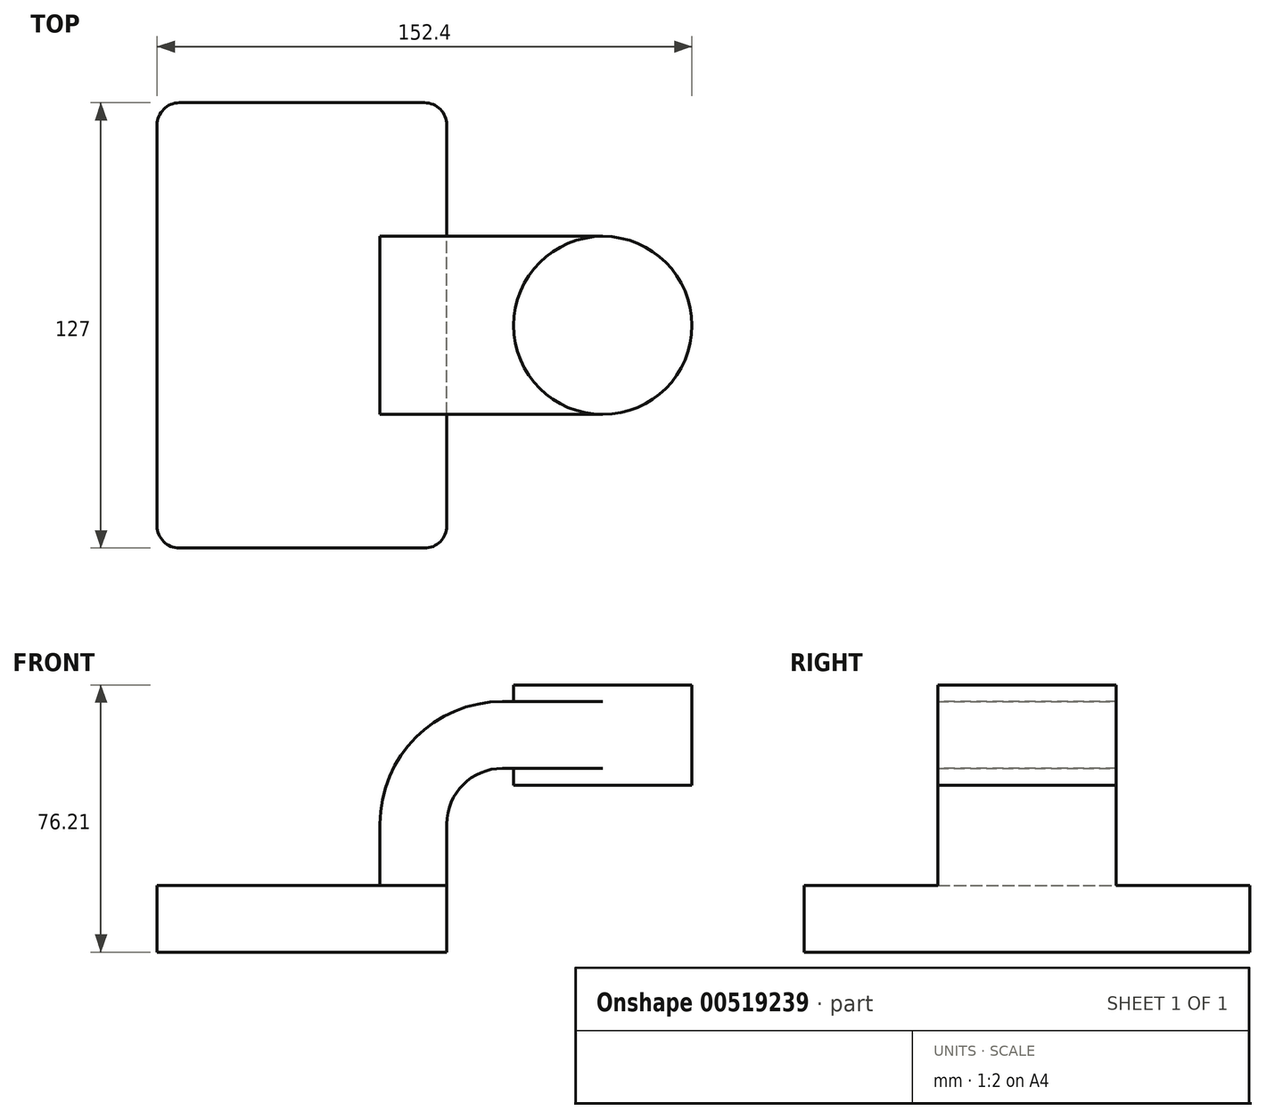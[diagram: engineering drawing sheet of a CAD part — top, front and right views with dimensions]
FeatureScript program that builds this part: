
annotation { "Feature Type Name" : "Feature", "Feature Type Description" : "" }
export const myFeature = defineFeature(function(context is Context, id is Id, definition is map)
    precondition{}
    {
        {
            var Q0;
            Q0=qCreatedBy(makeId("Front.planeOp"),FACE);
            var sketch = newSketch(context, id + "F0", { "sketchPlane" : qUnion([Q0])});
            skLineSegment(sketch, "E0.bottom", {"start": v(-41.27, -9.53) * mm, "end": v(41.28, -9.53) * mm});
            skLineSegment(sketch, "E0.top", {"start": v(-41.28, 9.53) * mm, "end": v(41.28, 9.53) * mm});
            skLineSegment(sketch, "E0.left", {"start": v(-41.28, -9.53) * mm, "end": v(-41.28, 9.53) * mm});
            skLineSegment(sketch, "E0.right", {"start": v(41.28, -9.53) * mm, "end": v(41.28, 9.53) * mm});
            skPoint(sketch, "E0.middle", {"position": v(0, 0) * mm});
            skLineSegment(sketch, "E1.bottom", {"start": v(60.33, 38.1) * mm, "end": v(111.12, 38.1) * mm});
            skLineSegment(sketch, "E1.top", {"start": v(60.32, 66.67) * mm, "end": v(111.12, 66.67) * mm});
            skLineSegment(sketch, "E1.left", {"start": v(60.32, 38.1) * mm, "end": v(60.32, 66.68) * mm});
            skLineSegment(sketch, "E1.right", {"start": v(111.12, 38.1) * mm, "end": v(111.12, 66.68) * mm});
            skPoint(sketch, "E1.middle", {"position": v(85.72, 52.39) * mm});
            skLineSegment(sketch, "E2", {"start": v(41.27, 9.52) * mm, "end": v(41.27, 27) * mm});
            skArc(sketch, "E3", {"start": v(41.27, 27) * mm, "mid": v(45.92, 38.23) * mm, "end": v(57.15, 42.88) * mm});
            skLineSegment(sketch, "E4", {"start": v(57.15, 42.88) * mm, "end": v(85.72, 42.88) * mm});
            skPoint(sketch, "E4.endSnap0", {"position": v(85.72, 38.1) * mm});
            skLineSegment(sketch, "E5.0", {"start": v(57.15, 61.93) * mm, "end": v(85.72, 61.93) * mm});
            skArc(sketch, "E5.1", {"start": v(22.22, 27) * mm, "mid": v(32.45, 51.7) * mm, "end": v(57.15, 61.93) * mm});
            skLineSegment(sketch, "E5.2", {"start": v(22.22, 9.52) * mm, "end": v(22.22, 27) * mm});
            skLineSegment(sketch, "E6", {"start": v(85.72, 66.67) * mm, "end": v(85.72, 38.1) * mm});
            skFitSpline(sketch, "E7", {"points": [v(-41.28, 9.53) * mm, v(57.15, 61.93) * mm], "startDerivative": vector(2.6, 90.34) * mm, "endDerivative": vector(107.06, -0.42) * mm});
            skSolve(sketch);
        }
        {
            var Q0;
            Q0=makeQuery(id+"F0.imprint","IMPRINT",FACE,{"disambiguationData":[TD([[makeQuery(id+"F0.imprint","IMPRINT",EDGE,{"derivedFrom":sQuery(id+"F0.wireOp",EDGE,"E0.bottom")}),1.0]])]});
            extrude(context, id + "F1", {"entities" : qUnion([Q0]), "endBound" : BoundingType.SYMMETRIC, "depth" : 127 * mm});
        }
        {
            var Q0;
            {var subQ1=sQuery(id+"F0.wireOp",EDGE,"E2");Q0=makeQuery(id+"F0.imprint","IMPRINT",FACE,{"disambiguationData":[TD([[makeQuery(id+"F0.imprint","IMPRINT",EDGE,{"derivedFrom":subQ1}),1.0]])]});}
            var Q1;
            {var subQ0=sQuery(id+"F0.wireOp",EDGE,"E4");var subQ1=sQuery(id+"F0.wireOp",EDGE,"E1.left");var subQ2=makeQuery(id+"F0.imprint","INTERSECT",VERTEX,{"derivedFrom":[subQ1,subQ0]});Q1=makeQuery(id+"F0.imprint","IMPRINT",FACE,{"disambiguationData":[TD([[makeQuery(id+"F0.imprint","IMPRINT",EDGE,{"disambiguationData":[TD([[subQ2,-1.0]])],"derivedFrom":subQ1}),-1.0]])]});}
            extrude(context, id + "F2", {"entities" : qUnion([Q0, Q1]), "operationType" : NewBodyOperationType.ADD, "endBound" : BoundingType.SYMMETRIC, "depth" : 50.8 * mm});
        }
        {
            var Q0;
            Q0=makeQuery(id+"F0.imprint","IMPRINT",FACE,{"disambiguationData":[TD([[makeQuery(id+"F0.imprint","IMPRINT",EDGE,{"derivedFrom":sQuery(id+"F0.wireOp",EDGE,"E5.1")}),1.0]])]});
            extrude(context, id + "F3", {"entities" : qUnion([Q0]), "operationType" : NewBodyOperationType.ADD, "endBound" : BoundingType.SYMMETRIC, "depth" : 15.88 * mm});
        }
        {
            var Q0;
            {var subQ0=sQuery(id+"F0.wireOp",EDGE,"E1.right");Q0=makeQuery(id+"F0.imprint","IMPRINT",FACE,{"disambiguationData":[TD([[makeQuery(id+"F0.imprint","IMPRINT",EDGE,{"derivedFrom":subQ0}),1.0]])]});}
            var Q1;
            Q1=sQuery(id+"F0.wireOp",EDGE,"E6");
            revolve(context, id + "F4", {"operationType" : NewBodyOperationType.ADD, "entities" : qUnion([Q0]), "axis" : qUnion([Q1]), "revolveType" : RevolveType.FULL});
        }
        {
            var Q0;
            Q0=makeQuery(id+"F1.opExtrude","CAP_EDGE",EDGE,{"disambiguationData":[OSD([sQuery(id+"F0.wireOp",EDGE,"E0.right")])],"isStart":false});
            var Q1;
            Q1=makeQuery(id+"F1.opExtrude","CAP_EDGE",EDGE,{"disambiguationData":[OSD([sQuery(id+"F0.wireOp",EDGE,"E0.left")])],"isStart":false});
            var Q2;
            Q2=makeQuery(id+"F1.opExtrude","CAP_EDGE",EDGE,{"disambiguationData":[OSD([sQuery(id+"F0.wireOp",EDGE,"E0.right")])],"isStart":true});
            var Q3;
            Q3=makeQuery(id+"F1.opExtrude","CAP_EDGE",EDGE,{"disambiguationData":[OSD([sQuery(id+"F0.wireOp",EDGE,"E0.left")])],"isStart":true});
            fillet(context, id + "F5", {"entities" : qUnion([Q0, Q1, Q2, Q3]), "radius" : 6.35 * mm, "tangentPropagation" : true, "allowEdgeOverflow" : false});
        }
    });
